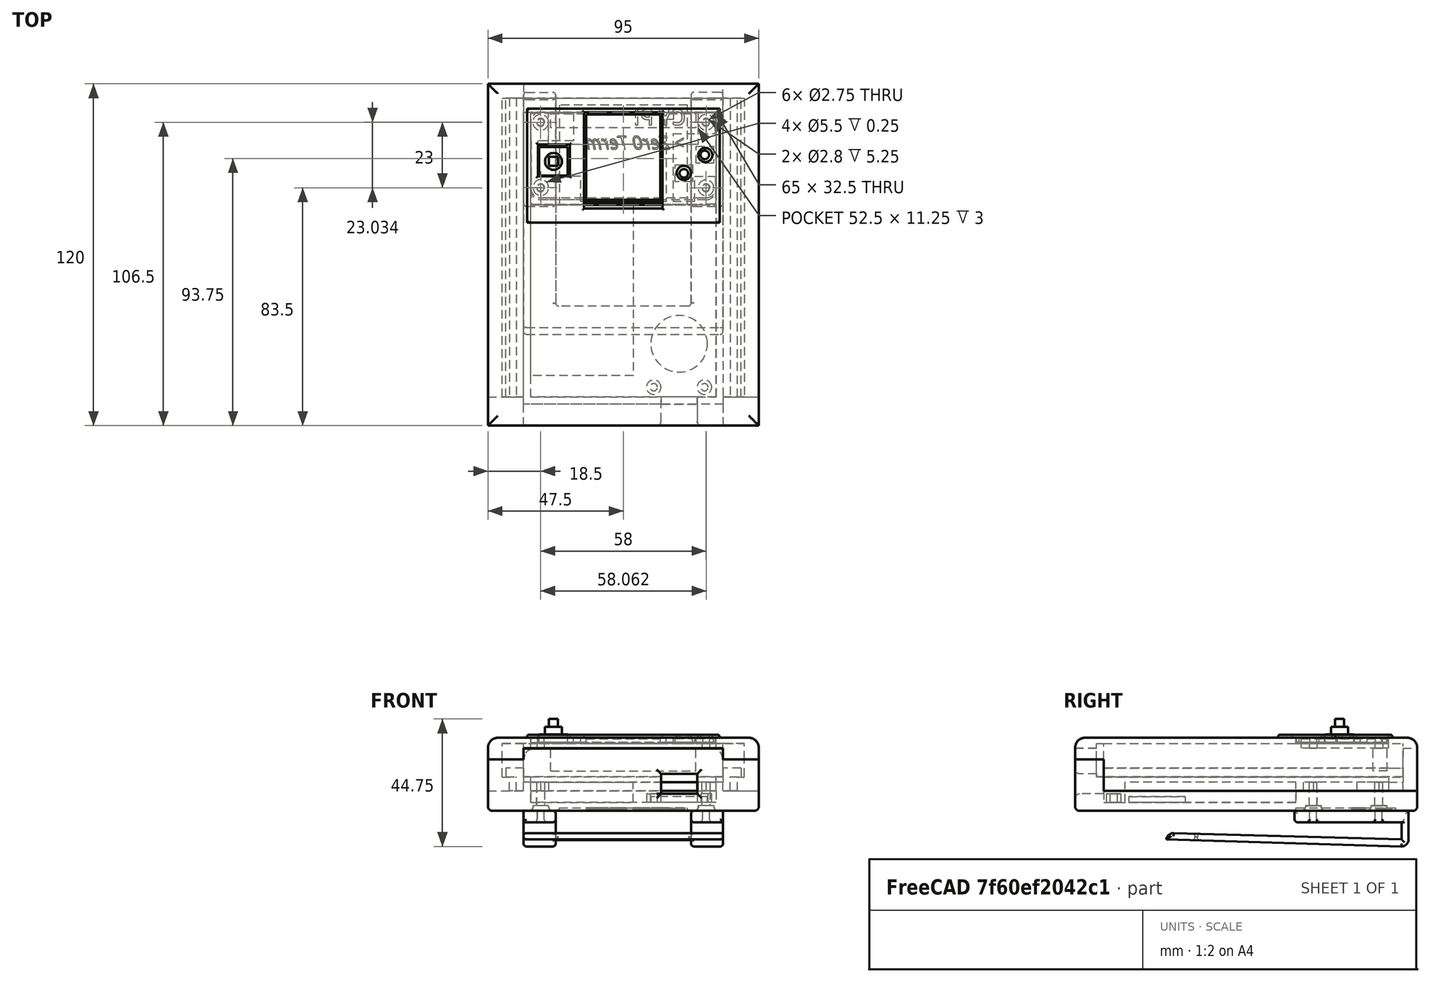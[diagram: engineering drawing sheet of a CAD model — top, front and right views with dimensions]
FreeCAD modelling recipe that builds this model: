
FCSTD DOCUMENT  (FreeCAD 0.18R4 (GitTag))
Label: ZeroDay-Dexk
License: All rights reserved
LicenseURL: http://en.wikipedia.org/wiki/All_rights_reserved
objects: Sketcher::SketchObject×37, PartDesign::Pad×28, PartDesign::Pocket×10, PartDesign::Fillet×9, PartDesign::Body×6, App::DocumentObjectGroup×3, Mesh::Feature×2, Part::Part2DObjectPython×2, Part::Extrusion×2, App::MeasureDistance×2
note: 132 computed .brp shape members not serialized (recipe doc carries the construction recipe); baked Part::Feature solids carry a one-line shape summary decoded from their .brp

FEATURE [Mesh::Feature] RaspberryPiZeroW
  Placement = pos=(0,0,0) rot=(1,0,0;1.5708rad)
FEATURE [Sketcher::SketchObject] Sketch
  MapMode = 5
  Placement = pos=(0,0,0) rot=(1,0,0;1.5708rad)
  Support = -> [XZ_Plane]
  sketch-geometry (18):
    g0: LineSegment [constr] StartX=0 StartY=0 StartZ=0 EndX=65 EndY=0 EndZ=0
    g1: LineSegment [constr] StartX=65 StartY=0 StartZ=0 EndX=65 EndY=30 EndZ=0
    g2: LineSegment [constr] StartX=65 StartY=30 StartZ=0 EndX=0 EndY=30 EndZ=0
    g3: LineSegment [constr] StartX=0 StartY=30 StartZ=0 EndX=0 EndY=0 EndZ=0
    g4: Circle CenterX=3.5 CenterY=26.5 CenterZ=0 NormalX=0 NormalY=0 NormalZ=1 AngleXU=0 Radius=1.375
    g5: Circle CenterX=61.5 CenterY=26.5 CenterZ=0 NormalX=0 NormalY=0 NormalZ=1 AngleXU=0 Radius=1.375
    g6: Circle CenterX=3.5 CenterY=3.5 CenterZ=0 NormalX=0 NormalY=0 NormalZ=1 AngleXU=0 Radius=1.375
    g7: Circle CenterX=61.5 CenterY=3.5 CenterZ=0 NormalX=0 NormalY=0 NormalZ=1 AngleXU=0 Radius=1.375
    g8: LineSegment StartX=6.25 StartY=0 StartZ=0 EndX=0 EndY=0 EndZ=0
    g9: LineSegment StartX=0 StartY=0 StartZ=0 EndX=0 EndY=30 EndZ=0
    g10: LineSegment StartX=0 StartY=30 StartZ=0 EndX=6.25 EndY=30 EndZ=0
    g11: LineSegment StartX=6.25 StartY=11.25 StartZ=0 EndX=6.25 EndY=0 EndZ=0
    g12: LineSegment StartX=6.25 StartY=30 StartZ=0 EndX=58.75 EndY=30 EndZ=0
    g13: LineSegment StartX=58.75 StartY=11.25 StartZ=0 EndX=6.25 EndY=11.25 EndZ=0
    g14: LineSegment StartX=65 StartY=0 StartZ=0 EndX=58.75 EndY=0 EndZ=0
    g15: LineSegment StartX=58.75 StartY=0 StartZ=0 EndX=58.75 EndY=11.25 EndZ=0
    g16: LineSegment StartX=58.75 StartY=30 StartZ=0 EndX=65 EndY=30 EndZ=0
    g17: LineSegment StartX=65 StartY=30 StartZ=0 EndX=65 EndY=0 EndZ=0
  constraints (38):
    c: Coincident(g0,g1)
    c: Coincident(g1,g2)
    c: Coincident(g2,g3)
    c: Coincident(g3,g0)
    c: Horizontal(g0)
    c: Horizontal(g2)
    c: Vertical(g1)
    c: Vertical(g3)
    c: DistanceY(g4,g2) = 3.5
    c: DistanceY(g0,g6) = 3.5
    c: DistanceY(g5,g1) = 3.5
    c: DistanceY(g0,g7) = 3.5
    c: DistanceX(g0,g6) = 3.5
    c: DistanceX(g2,g4) = 3.5
    c: DistanceX(g7,g0) = 3.5
    c: DistanceX(g5,g1) = 3.5
    c: Radius(g4) = 1.375
    c: Radius(g6) = 1.375
    c: Radius(g7) = 1.375
    c: Radius(g5) = 1.375
    c: Coincident(g8,g9)
    c: Coincident(g9,g10)
    c: Coincident(g11,g8)
    c: Horizontal(g8)
    c: Horizontal(g10)
    c: Vertical(g9)
    c: Vertical(g11)
    c: Horizontal(g12)
    c: Horizontal(g13)
    c: Coincident(g14,g15)
    c: Coincident(g16,g17)
    c: Coincident(g17,g14)
    c: Horizontal(g14)
    c: Horizontal(g16)
    c: Vertical(g15)
    c: Vertical(g17)
    c: PointOnObject(g15,g13)
    c: PointOnObject(g11,g13)
FEATURE [PartDesign::Pad] Pad
  Length = 3
  Length2 = 100
  Placement = pos=(0,0,0) rot=(1,0,0;1.5708rad)
  Profile = -> Sketch
  Type = 0
FEATURE [PartDesign::Fillet] Fillet
  Base = -> Pad [Edge5,Edge2,Edge14,Edge17]
  BaseFeature = -> Pad
  Placement = pos=(0,0,0) rot=(1,0,0;1.5708rad)
  Radius = 3.5
FEATURE [Sketcher::SketchObject] Sketch001
  ExternalGeometry = -> [Fillet]
  MapMode = 5
  Placement = pos=(0,-3,1.3e-15) rot=(1,0,0;1.5708rad)
  Support = -> [Fillet]
  sketch-geometry (8):
    g0: LineSegment StartX=-15 StartY=-10 StartZ=0 EndX=80 EndY=-10 EndZ=0
    g1: LineSegment StartX=80 StartY=-10 StartZ=0 EndX=80 EndY=110 EndZ=0
    g2: LineSegment StartX=80 StartY=110 StartZ=0 EndX=-15 EndY=110 EndZ=0
    g3: LineSegment StartX=-15 StartY=110 StartZ=0 EndX=-15 EndY=-10 EndZ=0
    g4: Circle CenterX=3.5 CenterY=26.5 CenterZ=0 NormalX=0 NormalY=0 NormalZ=1 AngleXU=0 Radius=1.375
    g5: Circle CenterX=3.5 CenterY=3.5 CenterZ=0 NormalX=0 NormalY=0 NormalZ=1 AngleXU=0 Radius=1.4
    g6: Circle CenterX=61.5 CenterY=3.5 CenterZ=0 NormalX=0 NormalY=0 NormalZ=1 AngleXU=0 Radius=1.4
    g7: Circle CenterX=61.5 CenterY=26.5 CenterZ=0 NormalX=0 NormalY=0 NormalZ=1 AngleXU=0 Radius=1.40357
  constraints (13):
    c: Coincident(g0,g1)
    c: Coincident(g1,g2)
    c: Coincident(g2,g3)
    c: Coincident(g3,g0)
    c: Horizontal(g0)
    c: Horizontal(g2)
    c: Vertical(g1)
    c: Vertical(g3)
    c: Radius(g-5) = 1.375
    c: Radius(g-5) = 1.375
    c: Radius(g4) = 1.375
    c: Distance(g0) = 95
    c: Distance(g1) = 120
FEATURE [PartDesign::Pad] Pad001
  BaseFeature = -> Fillet
  Length = 7
  Length2 = 100
  Placement = pos=(0,0,0) rot=(1,0,0;1.5708rad)
  Profile = -> Sketch001
  Type = 0
FEATURE [Sketcher::SketchObject] Sketch002
  ExternalGeometry = -> [Pad001]
  MapMode = 5
  Placement = pos=(0,-10,1e-14) rot=(1,0,0;1.5708rad)
  Support = -> [Pad001]
  sketch-geometry (4):
    g0: Circle CenterX=3.5 CenterY=3.5 CenterZ=0 NormalX=0 NormalY=0 NormalZ=1 AngleXU=0 Radius=2.75
    g1: Circle CenterX=3.55131 CenterY=26.4052 CenterZ=0 NormalX=0 NormalY=0 NormalZ=1 AngleXU=0 Radius=2.75
    g2: Circle CenterX=61.5 CenterY=26.5 CenterZ=0 NormalX=0 NormalY=0 NormalZ=1 AngleXU=0 Radius=2.75
    g3: Circle CenterX=61.5615 CenterY=3.46611 CenterZ=0 NormalX=0 NormalY=0 NormalZ=1 AngleXU=0 Radius=2.75
  constraints (4):
    c: Radius(g2) = 2.75
    c: Radius(g3) = 2.75
    c: Radius(g0) = 2.75
    c: Radius(g1) = 2.75
FEATURE [PartDesign::Pocket] Pocket
  BaseFeature = -> Pad001
  Length = 1.75
  Length2 = 100
  Placement = pos=(0,0,0) rot=(1,0,0;1.5708rad)
  Profile = -> Sketch002
  Type = 0
FEATURE [Sketcher::SketchObject] Sketch003
  MapMode = 5
  Placement = pos=(0,-3,3e-15) rot=(-1,0,0;1.5708rad)
  Support = -> [Pocket]
  sketch-geometry (4):
    g0: LineSegment StartX=0 StartY=-32.5 StartZ=0 EndX=65 EndY=-32.5 EndZ=0
    g1: LineSegment StartX=65 StartY=-32.5 StartZ=0 EndX=65 EndY=-100 EndZ=0
    g2: LineSegment StartX=65 StartY=-100 StartZ=0 EndX=0 EndY=-100 EndZ=0
    g3: LineSegment StartX=0 StartY=-100 StartZ=0 EndX=0 EndY=-32.5 EndZ=0
  constraints (8):
    c: Coincident(g0,g1)
    c: Coincident(g1,g2)
    c: Coincident(g2,g3)
    c: Coincident(g3,g0)
    c: Horizontal(g0)
    c: Horizontal(g2)
    c: Vertical(g1)
    c: Vertical(g3)
FEATURE [PartDesign::Pocket] Pocket001
  BaseFeature = -> Pocket
  Length = 4
  Length2 = 100
  Placement = pos=(0,0,0) rot=(1,0,0;1.5708rad)
  Profile = -> Sketch003
  Type = 0
FEATURE [Sketcher::SketchObject] Sketch004
  MapMode = 5
  Placement = pos=(0,-3,3e-15) rot=(-1,0,0;1.5708rad)
  Support = -> [Pocket001]
  sketch-geometry (14):
    g0: LineSegment StartX=0 StartY=5 StartZ=0 EndX=65 EndY=5 EndZ=0
    g1: LineSegment StartX=65 StartY=0 StartZ=0 EndX=0 EndY=0 EndZ=0
    g2: LineSegment StartX=80 StartY=-110 StartZ=0 EndX=-15 EndY=-110 EndZ=0
    g3: LineSegment StartX=-15 StartY=-110 StartZ=0 EndX=-15 EndY=-100 EndZ=0
    g4: LineSegment StartX=-15 StartY=-100 StartZ=0 EndX=-5 EndY=-100 EndZ=0
    g5: LineSegment StartX=80 StartY=-100 StartZ=0 EndX=80 EndY=-110 EndZ=0
    g6: LineSegment StartX=0 StartY=5 StartZ=0 EndX=-5 EndY=5 EndZ=0
    g7: LineSegment StartX=-5 StartY=5 StartZ=0 EndX=-5 EndY=-100 EndZ=0
    g8: LineSegment StartX=0 StartY=-100 StartZ=0 EndX=0 EndY=0 EndZ=0
    g9: LineSegment StartX=65 StartY=5 StartZ=0 EndX=70 EndY=5 EndZ=0
    g10: LineSegment StartX=70 StartY=5 StartZ=0 EndX=70 EndY=-100 EndZ=0
    g11: LineSegment StartX=65 StartY=-100 StartZ=0 EndX=65 EndY=0 EndZ=0
    g12: LineSegment StartX=70 StartY=-100 StartZ=0 EndX=80 EndY=-100 EndZ=0
    g13: LineSegment StartX=0 StartY=-100 StartZ=0 EndX=65 EndY=-100 EndZ=0
  constraints (24):
    c: Horizontal(g0)
    c: Horizontal(g1)
    c: Coincident(g2,g3)
    c: Coincident(g3,g4)
    c: Coincident(g12,g5)
    c: Coincident(g5,g2)
    c: Horizontal(g2)
    c: Horizontal(g4)
    c: Vertical(g3)
    c: Vertical(g5)
    c: Coincident(g6,g7)
    c: Horizontal(g6)
    c: Vertical(g7)
    c: Vertical(g8)
    c: Coincident(g9,g10)
    c: Horizontal(g9)
    c: Vertical(g10)
    c: Vertical(g11)
    c: PointOnObject(g12,g10)
    c: Tangent(g4,g12)
    c: PointOnObject(g4,g7)
    c: Tangent(g4,g13)
    c: PointOnObject(g8,g1)
    c: PointOnObject(g11,g1)
FEATURE [PartDesign::Pad] Pad002
  BaseFeature = -> Pocket001
  Length = 5
  Length2 = 100
  Placement = pos=(0,0,0) rot=(1,0,0;1.5708rad)
  Profile = -> Sketch004
  Type = 0
FEATURE [Sketcher::SketchObject] Sketch005
  MapMode = 5
  Placement = pos=(0,2,-4.4e-15) rot=(-1,0,0;1.5708rad)
  Support = -> [Pad002]
  sketch-geometry (12):
    g0: LineSegment StartX=75 StartY=5 StartZ=0 EndX=-10 EndY=5 EndZ=0
    g1: LineSegment StartX=-10 StartY=5 StartZ=0 EndX=-10 EndY=-100 EndZ=0
    g2: LineSegment StartX=-15 StartY=-100 StartZ=0 EndX=-10 EndY=-100 EndZ=0
    g3: LineSegment StartX=-15 StartY=-100 StartZ=0 EndX=-15 EndY=-110 EndZ=0
    g4: LineSegment StartX=-15 StartY=-110 StartZ=0 EndX=80 EndY=-110 EndZ=0
    g5: LineSegment StartX=80 StartY=-100 StartZ=0 EndX=80 EndY=-110 EndZ=0
    g6: LineSegment StartX=80 StartY=-100 StartZ=0 EndX=75 EndY=-100 EndZ=0
    g7: LineSegment StartX=75 StartY=-100 StartZ=0 EndX=75 EndY=5 EndZ=0
    g8: LineSegment StartX=-2.5 StartY=0 StartZ=0 EndX=67.5 EndY=0 EndZ=0
    g9: LineSegment StartX=67.5 StartY=0 StartZ=0 EndX=67.5 EndY=-102.5 EndZ=0
    g10: LineSegment StartX=67.5 StartY=-102.5 StartZ=0 EndX=-2.5 EndY=-102.5 EndZ=0
    g11: LineSegment StartX=-2.5 StartY=-102.5 StartZ=0 EndX=-2.5 EndY=0 EndZ=0
  constraints (8):
    c: Coincident(g8,g9)
    c: Coincident(g9,g10)
    c: Coincident(g10,g11)
    c: Coincident(g11,g8)
    c: Horizontal(g8)
    c: Horizontal(g10)
    c: Vertical(g9)
    c: Vertical(g11)
FEATURE [PartDesign::Pad] Pad003
  BaseFeature = -> Pad002
  Length = 3
  Length2 = 100
  Placement = pos=(0,0,0) rot=(1,0,0;1.5708rad)
  Profile = -> Sketch005
  Type = 0
FEATURE [Sketcher::SketchObject] Sketch006
  MapMode = 5
  Placement = pos=(0,5,-1.33e-14) rot=(-1,0,0;1.5708rad)
  Support = -> [Pad003]
  sketch-geometry (4):
    g0: LineSegment StartX=-2.5 StartY=0 StartZ=0 EndX=67.5 EndY=0 EndZ=0
    g1: LineSegment StartX=67.5 StartY=0 StartZ=0 EndX=67.5 EndY=5 EndZ=0
    g2: LineSegment StartX=67.5 StartY=5 StartZ=0 EndX=-2.5 EndY=5 EndZ=0
    g3: LineSegment StartX=-2.5 StartY=5 StartZ=0 EndX=-2.5 EndY=0 EndZ=0
  constraints (8):
    c: Coincident(g0,g1)
    c: Coincident(g1,g2)
    c: Coincident(g2,g3)
    c: Coincident(g3,g0)
    c: Horizontal(g0)
    c: Horizontal(g2)
    c: Vertical(g1)
    c: Vertical(g3)
FEATURE [PartDesign::Pocket] Pocket002
  BaseFeature = -> Pad003
  Length = 5
  Length2 = 100
  Placement = pos=(0,0,0) rot=(1,0,0;1.5708rad)
  Profile = -> Sketch006
  Type = 0
FEATURE [PartDesign::Fillet] Fillet001
  Base = -> Pocket002 [Face79]
  BaseFeature = -> Pocket002
  Placement = pos=(0,0,0) rot=(1,0,0;1.5708rad)
  Radius = 1.5
FEATURE [Sketcher::SketchObject] Sketch007
  MapMode = 5
  Placement = pos=(0,2.752e-13,110) rot=(0,0,1;3.14159rad)
  Support = -> [Fillet001]
FEATURE [Sketcher::SketchObject] Sketch008
  MapMode = 5
  Placement = pos=(0,-7,1.4e-14) rot=(-1,0,0;1.5708rad)
  Support = -> [Fillet001]
  sketch-geometry (9):
    g0: LineSegment [constr] StartX=63.5 StartY=-99.06 StartZ=0 EndX=40.64 EndY=-99.06 EndZ=0
    g1: LineSegment [constr] StartX=40.64 StartY=-99.06 StartZ=0 EndX=40.64 EndY=-63.5 EndZ=0
    g2: LineSegment [constr] StartX=40.64 StartY=-63.5 StartZ=0 EndX=63.5 EndY=-63.5 EndZ=0
    g3: LineSegment [constr] StartX=63.5 StartY=-63.5 StartZ=0 EndX=63.5 EndY=-99.06 EndZ=0
    g4: Circle CenterX=43.18 CenterY=-96.52 CenterZ=0 NormalX=0 NormalY=0 NormalZ=1 AngleXU=0 Radius=1.27
    g5: Circle CenterX=60.96 CenterY=-96.52 CenterZ=0 NormalX=0 NormalY=0 NormalZ=1 AngleXU=0 Radius=1.27
    g6: Circle CenterX=43.18 CenterY=-96.52 CenterZ=0 NormalX=0 NormalY=0 NormalZ=1 AngleXU=0 Radius=2.54
    g7: Circle CenterX=60.96 CenterY=-96.52 CenterZ=0 NormalX=0 NormalY=0 NormalZ=1 AngleXU=0 Radius=2.54
    g8: Circle CenterX=52.07 CenterY=-81.28 CenterZ=0 NormalX=0 NormalY=0 NormalZ=1 AngleXU=0 Radius=9.91902
  constraints (10):
    c: Coincident(g0,g1)
    c: Coincident(g1,g2)
    c: Coincident(g2,g3)
    c: Coincident(g3,g0)
    c: Horizontal(g0)
    c: Horizontal(g2)
    c: Vertical(g1)
    c: Vertical(g3)
    c: Radius(g5) = 1.27
    c: Radius(g4) = 1.27
FEATURE [PartDesign::Pad] Pad004
  BaseFeature = -> Fillet001
  Length = 2
  Length2 = 100
  Placement = pos=(0,0,0) rot=(1,0,0;1.5708rad)
  Profile = -> Sketch008
  Type = 0
FEATURE [PartDesign::Pad] Pad005
  BaseFeature = -> Pad004
  Length = 1
  Length2 = 100
  Placement = pos=(0,0,0) rot=(1,0,0;1.5708rad)
  Profile = -> Pad004 [Face95]
  Type = 0
FEATURE [PartDesign::Pad] Pad006
  BaseFeature = -> Pad005
  Length = 1
  Length2 = 100
  Placement = pos=(0,0,0) rot=(1,0,0;1.5708rad)
  Profile = -> Pad005 [Face94]
  Type = 0
FEATURE [Sketcher::SketchObject] Sketch009
  MapMode = 5
  Placement = pos=(0,2,-4.4e-15) rot=(-1,0,0;1.5708rad)
  Support = -> [Pad006]
  sketch-geometry (8):
    g0: LineSegment [constr] StartX=40.64 StartY=-99.06 StartZ=0 EndX=63.5 EndY=-99.06 EndZ=0
    g1: LineSegment [constr] StartX=63.5 StartY=-99.06 StartZ=0 EndX=63.5 EndY=-58.42 EndZ=0
    g2: LineSegment [constr] StartX=63.5 StartY=-58.42 StartZ=0 EndX=40.64 EndY=-58.42 EndZ=0
    g3: LineSegment [constr] StartX=40.64 StartY=-58.42 StartZ=0 EndX=40.64 EndY=-99.06 EndZ=0
    g4: LineSegment StartX=45.72 StartY=-99.06 StartZ=0 EndX=58.42 EndY=-99.06 EndZ=0
    g5: LineSegment StartX=58.42 StartY=-99.06 StartZ=0 EndX=58.42 EndY=-111.76 EndZ=0
    g6: LineSegment StartX=58.42 StartY=-111.76 StartZ=0 EndX=45.72 EndY=-111.76 EndZ=0
    g7: LineSegment StartX=45.72 StartY=-111.76 StartZ=0 EndX=45.72 EndY=-99.06 EndZ=0
  constraints (16):
    c: Coincident(g0,g1)
    c: Coincident(g1,g2)
    c: Coincident(g2,g3)
    c: Coincident(g3,g0)
    c: Horizontal(g0)
    c: Horizontal(g2)
    c: Vertical(g1)
    c: Vertical(g3)
    c: Coincident(g4,g5)
    c: Coincident(g5,g6)
    c: Coincident(g6,g7)
    c: Coincident(g7,g4)
    c: Horizontal(g4)
    c: Horizontal(g6)
    c: Vertical(g5)
    c: Vertical(g7)
FEATURE [PartDesign::Pocket] Pocket003
  BaseFeature = -> Pad006
  Length = 6
  Length2 = 1
  Placement = pos=(0,0,0) rot=(1,0,0;1.5708rad)
  Profile = -> Sketch009
  Type = 4
FEATURE [PartDesign::Fillet] Fillet002
  Base = -> Pocket003 [Edge49,Edge9,Edge32,Edge85]
  BaseFeature = -> Pocket003
  Placement = pos=(0,0,0) rot=(1,0,0;1.5708rad)
  Radius = 1.5
FEATURE [Sketcher::SketchObject] Sketch010
  MapMode = 5
  Placement = pos=(0,5,-1.33e-14) rot=(-1,0,0;1.5708rad)
  Support = -> [Fillet002]
  sketch-geometry (12):
    g0: LineSegment StartX=-15 StartY=-100 StartZ=0 EndX=-2.5 EndY=-100 EndZ=0
    g1: LineSegment StartX=-2.5 StartY=-100 StartZ=0 EndX=-2.5 EndY=-110 EndZ=0
    g2: LineSegment StartX=-2.5 StartY=-110 StartZ=0 EndX=-15 EndY=-110 EndZ=0
    g3: LineSegment StartX=-15 StartY=-110 StartZ=0 EndX=-15 EndY=-100 EndZ=0
    g4: LineSegment StartX=-2.5 StartY=-102.5 StartZ=0 EndX=67.5 EndY=-102.5 EndZ=0
    g5: LineSegment StartX=67.5 StartY=-102.5 StartZ=0 EndX=67.5 EndY=-110 EndZ=0
    g6: LineSegment StartX=67.5 StartY=-110 StartZ=0 EndX=-2.5 EndY=-110 EndZ=0
    g7: LineSegment StartX=-2.5 StartY=-110 StartZ=0 EndX=-2.5 EndY=-102.5 EndZ=0
    g8: LineSegment StartX=67.5 StartY=-100 StartZ=0 EndX=80 EndY=-100 EndZ=0
    g9: LineSegment StartX=80 StartY=-100 StartZ=0 EndX=80 EndY=-110 EndZ=0
    g10: LineSegment StartX=80 StartY=-110 StartZ=0 EndX=67.5 EndY=-110 EndZ=0
    g11: LineSegment StartX=67.5 StartY=-110 StartZ=0 EndX=67.5 EndY=-100 EndZ=0
  constraints (24):
    c: Coincident(g0,g1)
    c: Coincident(g1,g2)
    c: Coincident(g2,g3)
    c: Coincident(g3,g0)
    c: Horizontal(g0)
    c: Horizontal(g2)
    c: Vertical(g1)
    c: Vertical(g3)
    c: Coincident(g4,g5)
    c: Coincident(g5,g6)
    c: Coincident(g6,g7)
    c: Coincident(g7,g4)
    c: Horizontal(g4)
    c: Horizontal(g6)
    c: Vertical(g5)
    c: Vertical(g7)
    c: Coincident(g8,g9)
    c: Coincident(g9,g10)
    c: Coincident(g10,g11)
    c: Coincident(g11,g8)
    c: Horizontal(g8)
    c: Horizontal(g10)
    c: Vertical(g9)
    c: Vertical(g11)
FEATURE [PartDesign::Pad] Pad007
  BaseFeature = -> Fillet002
  Length = 3
  Length2 = 100
  Placement = pos=(0,0,0) rot=(1,0,0;1.5708rad)
  Profile = -> Sketch010
  Type = 0
FEATURE [Sketcher::SketchObject] Sketch011
  MapMode = 5
  Support = -> [XY_Plane001]
  sketch-geometry (10):
    g0: LineSegment StartX=0 StartY=0 StartZ=0 EndX=95 EndY=0 EndZ=0
    g1: LineSegment StartX=95 StartY=0 StartZ=0 EndX=95 EndY=-5 EndZ=0
    g2: LineSegment StartX=86.25 StartY=-5 StartZ=0 EndX=8.75 EndY=-5 EndZ=0
    g3: LineSegment StartX=0 StartY=-5 StartZ=0 EndX=0 EndY=0 EndZ=0
    g4: LineSegment StartX=86.25 StartY=-5 StartZ=0 EndX=86.25 EndY=-110 EndZ=0
    g5: LineSegment StartX=86.25 StartY=-110 StartZ=0 EndX=95 EndY=-110 EndZ=0
    g6: LineSegment StartX=95 StartY=-110 StartZ=0 EndX=95 EndY=-5 EndZ=0
    g7: LineSegment StartX=0 StartY=-5 StartZ=0 EndX=0 EndY=-110 EndZ=0
    g8: LineSegment StartX=0 StartY=-110 StartZ=0 EndX=8.75 EndY=-110 EndZ=0
    g9: LineSegment StartX=8.75 StartY=-110 StartZ=0 EndX=8.75 EndY=-5 EndZ=0
  constraints (18):
    c: Coincident(g0,g1)
    c: Coincident(g3,g0)
    c: Horizontal(g0)
    c: Horizontal(g2)
    c: Vertical(g1)
    c: Vertical(g3)
    c: Coincident(g0,g-1)
    c: Coincident(g4,g5)
    c: Coincident(g5,g6)
    c: Horizontal(g5)
    c: Vertical(g4)
    c: Vertical(g6)
    c: Coincident(g7,g8)
    c: Coincident(g8,g9)
    c: Horizontal(g8)
    c: Vertical(g7)
    c: Vertical(g9)
    c: PointOnObject(g9,g2)
FEATURE [PartDesign::Pad] Pad008
  Length = 4.8
  Length2 = 100
  Profile = -> Sketch011
  Type = 0
FEATURE [Sketcher::SketchObject] Sketch012
  MapMode = 5
  Placement = pos=(0,0,4.8) rot=(0,0,1;0rad)
  Support = -> [Pad008]
  sketch-geometry (12):
    g0: LineSegment StartX=0 StartY=0 StartZ=0 EndX=5 EndY=0 EndZ=0
    g1: LineSegment StartX=5 StartY=0 StartZ=0 EndX=5 EndY=-110 EndZ=0
    g2: LineSegment StartX=5 StartY=-110 StartZ=0 EndX=0 EndY=-110 EndZ=0
    g3: LineSegment StartX=0 StartY=-110 StartZ=0 EndX=0 EndY=0 EndZ=0
    g4: LineSegment StartX=90 StartY=-110 StartZ=0 EndX=95 EndY=-110 EndZ=0
    g5: LineSegment StartX=95 StartY=-110 StartZ=0 EndX=95 EndY=-5 EndZ=0
    g6: LineSegment StartX=95 StartY=-5 StartZ=0 EndX=90 EndY=-5 EndZ=0
    g7: LineSegment StartX=90 StartY=-5 StartZ=0 EndX=90 EndY=-110 EndZ=0
    g8: LineSegment StartX=95 StartY=0 StartZ=0 EndX=5 EndY=0 EndZ=0
    g9: LineSegment StartX=5 StartY=0 StartZ=0 EndX=5 EndY=-5 EndZ=0
    g10: LineSegment StartX=5 StartY=-5 StartZ=0 EndX=95 EndY=-5 EndZ=0
    g11: LineSegment StartX=95 StartY=-5 StartZ=0 EndX=95 EndY=0 EndZ=0
  constraints (26):
    c: Coincident(g0,g1)
    c: Coincident(g1,g2)
    c: Coincident(g2,g3)
    c: Coincident(g3,g0)
    c: Horizontal(g0)
    c: Horizontal(g2)
    c: Vertical(g1)
    c: Vertical(g3)
    c: Coincident(g0,g-1)
    c: Coincident(g4,g5)
    c: Coincident(g5,g6)
    c: Coincident(g6,g7)
    c: Coincident(g7,g4)
    c: Horizontal(g4)
    c: Horizontal(g6)
    c: Vertical(g5)
    c: Vertical(g7)
    c: Coincident(g8,g9)
    c: Coincident(g9,g10)
    c: Coincident(g10,g11)
    c: Coincident(g11,g8)
    c: Horizontal(g8)
    c: Horizontal(g10)
    c: Vertical(g9)
    c: Vertical(g11)
    c: PointOnObject(g9,g1)
FEATURE [PartDesign::Pad] Pad009
  BaseFeature = -> Pad008
  Length = 0.2
  Length2 = 100
  Profile = -> Sketch012
  Type = 0
FEATURE [PartDesign::Pad] Pad010
  BaseFeature = -> Pad009
  Length = 6
  Length2 = 100
  Profile = -> Pad009 [Face16]
  Type = 0
FEATURE [Mesh::Feature] _0x2_pin_header  label="20x2 pin header"
  Placement = pos=(32.5,-3,1.5) rot=(0,0,1;4.71239rad)
FEATURE [Sketcher::SketchObject] Sketch013
  MapMode = 5
  Support = -> [XY_Plane002]
  sketch-geometry (4):
    g0: LineSegment StartX=7 StartY=-0.5 StartZ=0 EndX=58 EndY=-0.5 EndZ=0
    g1: LineSegment StartX=58 StartY=-0.5 StartZ=0 EndX=58 EndY=-5.5 EndZ=0
    g2: LineSegment StartX=58 StartY=-5.5 StartZ=0 EndX=7 EndY=-5.5 EndZ=0
    g3: LineSegment StartX=7 StartY=-5.5 StartZ=0 EndX=7 EndY=-0.5 EndZ=0
  constraints (8):
    c: Coincident(g0,g1)
    c: Coincident(g1,g2)
    c: Coincident(g2,g3)
    c: Coincident(g3,g0)
    c: Horizontal(g0)
    c: Horizontal(g2)
    c: Vertical(g1)
    c: Vertical(g3)
FEATURE [PartDesign::Pad] Pad011
  Length = 8
  Length2 = 100
  Profile = -> Sketch013
  Type = 0
FEATURE [Sketcher::SketchObject] Sketch014
  MapMode = 5
  Placement = pos=(0,0,8) rot=(0,0,1;0rad)
  Support = -> [Pad011]
  sketch-geometry (8):
    g0: LineSegment StartX=0 StartY=0 StartZ=0 EndX=65 EndY=0 EndZ=0
    g1: LineSegment StartX=65 StartY=0 StartZ=0 EndX=65 EndY=-30.7 EndZ=0
    g2: LineSegment StartX=65 StartY=-30.7 StartZ=0 EndX=0 EndY=-30.7 EndZ=0
    g3: LineSegment StartX=0 StartY=-30.7 StartZ=0 EndX=0 EndY=0 EndZ=0
    g4: Circle CenterX=3.5 CenterY=-3.5 CenterZ=0 NormalX=0 NormalY=0 NormalZ=1 AngleXU=0 Radius=1.375
    g5: Circle CenterX=61.5 CenterY=-3.5 CenterZ=0 NormalX=0 NormalY=0 NormalZ=1 AngleXU=0 Radius=1.375
    g6: Circle CenterX=61.5 CenterY=-26.5 CenterZ=0 NormalX=0 NormalY=0 NormalZ=1 AngleXU=0 Radius=1.375
    g7: Circle CenterX=3.5 CenterY=-26.5 CenterZ=0 NormalX=0 NormalY=0 NormalZ=1 AngleXU=0 Radius=1.375
  constraints (23):
    c: Coincident(g0,g1)
    c: Coincident(g1,g2)
    c: Coincident(g2,g3)
    c: Coincident(g3,g0)
    c: Horizontal(g0)
    c: Horizontal(g2)
    c: Vertical(g1)
    c: Vertical(g3)
    c: Coincident(g0,g-1)
    c: Distance(g1) = 30.7
    c: Radius(g7) = 1.375
    c: Radius(g4) = 1.375
    c: Radius(g5) = 1.375
    c: Radius(g6) = 1.375
    c: DistanceX(g0,g4) = 3.5
    c: DistanceX(g5,g0) = 3.5
    c: DistanceX(g6,g1) = 3.5
    c: DistanceX(g2,g7) = 3.5
    c: Distance(g0) = 65
    c: DistanceY(g5,g0) = 3.5
    c: DistanceY(g4,g0) = 3.5
    c: DistanceY(g1,g6) = 4.2
    c: DistanceY(g2,g7) = 4.2
FEATURE [PartDesign::Pad] Pad012
  BaseFeature = -> Pad011
  Length = 1.651
  Length2 = 100
  Profile = -> Sketch014
  Type = 0
FEATURE [PartDesign::Fillet] Fillet003
  Base = -> Pad012 [Edge1,Edge5,Edge8,Edge2]
  BaseFeature = -> Pad012
  Radius = 3.5
FEATURE [Sketcher::SketchObject] Sketch015
  MapMode = 5
  Placement = pos=(0,-10,1e-14) rot=(1,0,0;1.5708rad)
  Support = -> [Pad007]
  sketch-geometry (4):
    g0: LineSegment StartX=55 StartY=-2.5 StartZ=0 EndX=10 EndY=-2.5 EndZ=0
    g1: LineSegment StartX=10 StartY=-2.5 StartZ=0 EndX=10 EndY=32.5 EndZ=0
    g2: LineSegment StartX=10 StartY=32.5 StartZ=0 EndX=55 EndY=32.5 EndZ=0
    g3: LineSegment StartX=55 StartY=32.5 StartZ=0 EndX=55 EndY=-2.5 EndZ=0
  constraints (8):
    c: Coincident(g0,g1)
    c: Coincident(g1,g2)
    c: Coincident(g2,g3)
    c: Coincident(g3,g0)
    c: Horizontal(g0)
    c: Horizontal(g2)
    c: Vertical(g1)
    c: Vertical(g3)
FEATURE [PartDesign::Pocket] Pocket004
  BaseFeature = -> Pad007
  Length = 1
  Length2 = 100
  Placement = pos=(0,0,0) rot=(1,0,0;1.5708rad)
  Profile = -> Sketch015
  Type = 0
FEATURE [Sketcher::SketchObject] Sketch017
  ExternalGeometry = -> [Fillet003]
  MapMode = 5
  Placement = pos=(0,0,9.651) rot=(0,0,1;0rad)
  Support = -> [Fillet003]
  sketch-geometry (5):
    g0: LineSegment StartX=3 StartY=-22.24 StartZ=0 EndX=13 EndY=-22.24 EndZ=0
    g1: LineSegment StartX=13 StartY=-22.24 StartZ=0 EndX=13 EndY=-12.24 EndZ=0
    g2: LineSegment StartX=13 StartY=-12.24 StartZ=0 EndX=3 EndY=-12.24 EndZ=0
    g3: LineSegment StartX=3 StartY=-12.24 StartZ=0 EndX=3 EndY=-22.24 EndZ=0
    g4: GeomPoint X=8 Y=-17.24 Z=0
  constraints (14):
    c: Coincident(g0,g1)
    c: Coincident(g1,g2)
    c: Coincident(g2,g3)
    c: Coincident(g3,g0)
    c: Horizontal(g0)
    c: Horizontal(g2)
    c: Vertical(g1)
    c: Vertical(g3)
    c: Distance(g1) = 10
    c: Distance(g0) = 10
    c: DistanceX(g4,g1) = 5
    c: DistanceX(g-4,g4) = 8
    c: DistanceY(g0,g4) = 5
    c: DistanceY(g-3,g4) = 13.46
FEATURE [PartDesign::Pad] Pad014
  BaseFeature = -> Fillet003
  Length = 3.15
  Length2 = 100
  Profile = -> Sketch017
  Type = 0
FEATURE [Sketcher::SketchObject] Sketch018
  ExternalGeometry = -> [Pad014]
  MapMode = 5
  Placement = pos=(0,0,12.801) rot=(0,0,1;0rad)
  Support = -> [Pad014]
  sketch-geometry (1):
    g0: Circle CenterX=8 CenterY=-17.24 CenterZ=0 NormalX=0 NormalY=0 NormalZ=1 AngleXU=0 Radius=2.975
  constraints (3):
    c: Radius(g0) = 2.975
    c: DistanceY(g0,g-4) = 5
    c: DistanceX(g0,g-4) = 5
FEATURE [PartDesign::Pad] Pad015
  BaseFeature = -> Pad014
  Length = 2.65
  Length2 = 100
  Profile = -> Sketch018
  Type = 0
FEATURE [Sketcher::SketchObject] Sketch019
  ExternalGeometry = -> [Pad015]
  MapMode = 5
  Placement = pos=(0,0,15.451) rot=(0,0,1;0rad)
  Support = -> [Pad015]
  sketch-geometry (4):
    g0: LineSegment StartX=6.4 StartY=-15.64 StartZ=0 EndX=9.6 EndY=-15.64 EndZ=0
    g1: LineSegment StartX=9.6 StartY=-15.64 StartZ=0 EndX=9.6 EndY=-18.84 EndZ=0
    g2: LineSegment StartX=9.6 StartY=-18.84 StartZ=0 EndX=6.4 EndY=-18.84 EndZ=0
    g3: LineSegment StartX=6.4 StartY=-18.84 StartZ=0 EndX=6.4 EndY=-15.64 EndZ=0
  constraints (12):
    c: Coincident(g0,g1)
    c: Coincident(g1,g2)
    c: Coincident(g2,g3)
    c: Coincident(g3,g0)
    c: Horizontal(g0)
    c: Horizontal(g2)
    c: Vertical(g1)
    c: Vertical(g3)
    c: Distance(g1) = 3.2
    c: Distance(g0) = 3.2
    c: DistanceY(g-3,g0) = 1.6
    c: DistanceX(g0,g-3) = 1.6
FEATURE [PartDesign::Pad] Pad016
  BaseFeature = -> Pad015
  Length = 2.8
  Length2 = 100
  Profile = -> Sketch019
  Type = 0
FEATURE [Sketcher::SketchObject] Sketch020
  ExternalGeometry = -> [Pad016]
  MapMode = 5
  Placement = pos=(0,0,9.651) rot=(0,0,1;0rad)
  Support = -> [Pad016]
  sketch-geometry (8):
    g0: LineSegment StartX=58.09 StartY=-11.95 StartZ=0 EndX=64.09 EndY=-11.95 EndZ=0
    g1: LineSegment StartX=64.09 StartY=-11.95 StartZ=0 EndX=64.09 EndY=-17.95 EndZ=0
    g2: LineSegment StartX=64.09 StartY=-17.95 StartZ=0 EndX=58.09 EndY=-17.95 EndZ=0
    g3: LineSegment StartX=58.09 StartY=-17.95 StartZ=0 EndX=58.09 EndY=-11.95 EndZ=0
    g4: LineSegment StartX=50.75 StartY=-18.43 StartZ=0 EndX=56.75 EndY=-18.43 EndZ=0
    g5: LineSegment StartX=56.75 StartY=-18.43 StartZ=0 EndX=56.75 EndY=-24.43 EndZ=0
    g6: LineSegment StartX=56.75 StartY=-24.43 StartZ=0 EndX=50.75 EndY=-24.43 EndZ=0
    g7: LineSegment StartX=50.75 StartY=-24.43 StartZ=0 EndX=50.75 EndY=-18.43 EndZ=0
  constraints (24):
    c: Coincident(g0,g1)
    c: Coincident(g1,g2)
    c: Coincident(g2,g3)
    c: Coincident(g3,g0)
    c: Horizontal(g0)
    c: Horizontal(g2)
    c: Vertical(g1)
    c: Vertical(g3)
    c: Coincident(g4,g5)
    c: Coincident(g5,g6)
    c: Coincident(g6,g7)
    c: Coincident(g7,g4)
    c: Horizontal(g4)
    c: Horizontal(g6)
    c: Vertical(g5)
    c: Vertical(g7)
    c: Distance(g5) = 6
    c: Distance(g6) = 6
    c: Distance(g3) = 6
    c: Distance(g0) = 6
    c: DistanceX(g0,g-3) = 0.91
    c: DistanceY(g-4,g1) = 12.75
    c: DistanceY(g-4,g5) = 6.27
    c: DistanceX(g4,g-3) = 8.25
FEATURE [PartDesign::Pad] Pad017
  BaseFeature = -> Pad016
  Length = 1.8
  Length2 = 100
  Profile = -> Sketch020
  Type = 0
FEATURE [Sketcher::SketchObject] Sketch021
  ExternalGeometry = -> [Pad017]
  MapMode = 5
  Placement = pos=(0,0,11.451) rot=(0,0,1;0rad)
  Support = -> [Pad017]
  sketch-geometry (2):
    g0: Circle CenterX=53.75 CenterY=-21.43 CenterZ=0 NormalX=0 NormalY=0 NormalZ=1 AngleXU=0 Radius=1.5
    g1: Circle CenterX=61.09 CenterY=-14.95 CenterZ=0 NormalX=0 NormalY=0 NormalZ=1 AngleXU=0 Radius=1.5
  constraints (6):
    c: Radius(g0) = 1.5
    c: Radius(g1) = 1.5
    c: DistanceX(g-6,g0) = 3
    c: DistanceX(g-4,g1) = 3
    c: DistanceY(g-6,g0) = 3
    c: DistanceY(g-4,g1) = 3
FEATURE [PartDesign::Pad] Pad018
  BaseFeature = -> Pad017
  Length = 1.3
  Length2 = 100
  Profile = -> Sketch021
  Type = 0
FEATURE [Sketcher::SketchObject] Sketch022
  ExternalGeometry = -> [Pad018]
  MapMode = 5
  Placement = pos=(0,0,9.651) rot=(0,0,1;0rad)
  Support = -> [Pad018]
  sketch-geometry (4):
    g0: LineSegment StartX=19.51 StartY=-0.7 StartZ=0 EndX=45.51 EndY=-0.7 EndZ=0
    g1: LineSegment StartX=45.51 StartY=-0.7 StartZ=0 EndX=45.51 EndY=-30.7 EndZ=0
    g2: LineSegment StartX=45.51 StartY=-30.7 StartZ=0 EndX=19.51 EndY=-30.7 EndZ=0
    g3: LineSegment StartX=19.51 StartY=-30.7 StartZ=0 EndX=19.51 EndY=-0.7 EndZ=0
  constraints (12):
    c: Coincident(g0,g1)
    c: Coincident(g1,g2)
    c: Coincident(g2,g3)
    c: Coincident(g3,g0)
    c: Horizontal(g0)
    c: Horizontal(g2)
    c: Vertical(g1)
    c: Vertical(g3)
    c: DistanceX(g-3,g2) = 19.51
    c: DistanceY(g-4,g2) = 0
    c: Distance(g1) = 30
    c: Distance(g0) = 26
FEATURE [PartDesign::Pad] Pad019
  BaseFeature = -> Pad018
  Length = 1.65
  Length2 = 100
  Profile = -> Sketch022
  Type = 0
FEATURE [PartDesign::Body] Body002  label="1.3 Color TFT Bonnet"
  Group = -> [Sketch013,Pad011,Sketch014,Pad012,Fillet003,Sketch017,Pad014,Sketch018,Pad015,Sketch019,Pad016,Sketch020,Pad017,Sketch021,Pad018,Sketch022,Pad019]
  Origin = -> Origin002
  Placement = pos=(0,0,4) rot=(0,0,1;0rad)
  Tip = -> Pad019
FEATURE [Sketcher::SketchObject] Sketch023
  MapMode = 5
  Support = -> [XY_Plane003]
  sketch-geometry (4):
    g0: LineSegment StartX=0 StartY=0 StartZ=0 EndX=36 EndY=0 EndZ=0
    g1: LineSegment StartX=36 StartY=0 StartZ=0 EndX=36 EndY=-60 EndZ=0
    g2: LineSegment StartX=36 StartY=-60 StartZ=0 EndX=0 EndY=-60 EndZ=0
    g3: LineSegment StartX=0 StartY=-60 StartZ=0 EndX=0 EndY=0 EndZ=0
  constraints (11):
    c: Coincident(g0,g1)
    c: Coincident(g1,g2)
    c: Coincident(g2,g3)
    c: Coincident(g3,g0)
    c: Horizontal(g0)
    c: Horizontal(g2)
    c: Vertical(g1)
    c: Vertical(g3)
    c: Coincident(g0,g-1)
    c: Distance(g2) = 36
    c: Distance(g1) = 60
FEATURE [PartDesign::Pad] Pad020
  Length = 7
  Length2 = 100
  Profile = -> Sketch023
  Type = 0
FEATURE [PartDesign::Body] Body003  label="Lipo 2000mAh"
  Group = -> [Sketch023,Pad020]
  Origin = -> Origin003
  Placement = pos=(0,-32.5,-7) rot=(0,0,1;0rad)
  Tip = -> Pad020
FEATURE [Sketcher::SketchObject] Sketch024
  MapMode = 5
  Placement = pos=(0,0,11) rot=(0,0,1;0rad)
  Support = -> [Pad010]
  sketch-geometry (12):
    g0: LineSegment StartX=0 StartY=0 StartZ=0 EndX=95 EndY=0 EndZ=0
    g1: LineSegment StartX=95 StartY=0 StartZ=0 EndX=95 EndY=-120 EndZ=0
    g2: LineSegment StartX=95 StartY=-120 StartZ=0 EndX=0 EndY=-120 EndZ=0
    g3: LineSegment StartX=0 StartY=-120 StartZ=0 EndX=0 EndY=0 EndZ=0
    g4: LineSegment StartX=5 StartY=-5 StartZ=0 EndX=90 EndY=-5 EndZ=0
    g5: LineSegment StartX=90 StartY=-5 StartZ=0 EndX=90 EndY=-110 EndZ=0
    g6: LineSegment StartX=90 StartY=-110 StartZ=0 EndX=82.5 EndY=-110 EndZ=0
    g7: LineSegment StartX=82.5 StartY=-110 StartZ=0 EndX=82.5 EndY=-112.5 EndZ=0
    g8: LineSegment StartX=82.5 StartY=-112.5 StartZ=0 EndX=12.5 EndY=-112.5 EndZ=0
    g9: LineSegment StartX=12.5 StartY=-112.5 StartZ=0 EndX=12.5 EndY=-110 EndZ=0
    g10: LineSegment StartX=12.5 StartY=-110 StartZ=0 EndX=5 EndY=-110 EndZ=0
    g11: LineSegment StartX=5 StartY=-110 StartZ=0 EndX=5 EndY=-5 EndZ=0
  constraints (25):
    c: Coincident(g0,g1)
    c: Coincident(g1,g2)
    c: Coincident(g2,g3)
    c: Coincident(g3,g0)
    c: Horizontal(g0)
    c: Horizontal(g2)
    c: Vertical(g1)
    c: Vertical(g3)
    c: Coincident(g0,g-1)
    c: Horizontal(g4)
    c: Coincident(g5,g4)
    c: Vertical(g5)
    c: Coincident(g6,g5)
    c: Horizontal(g6)
    c: Coincident(g7,g6)
    c: Vertical(g7)
    c: Coincident(g8,g7)
    c: Horizontal(g8)
    c: Coincident(g9,g8)
    c: Vertical(g9)
    c: Coincident(g10,g9)
    c: Horizontal(g10)
    c: Coincident(g11,g10)
    c: Coincident(g11,g4)
    c: Vertical(g11)
FEATURE [PartDesign::Pad] Pad021
  BaseFeature = -> Pad010
  Length = 5.67
  Length2 = 100
  Profile = -> Sketch024
  Type = 0
FEATURE [Sketcher::SketchObject] Sketch025
  MapMode = 5
  Placement = pos=(0,0,16.67) rot=(0,0,1;0rad)
  Support = -> [Pad021]
  sketch-geometry (12):
    g0: LineSegment StartX=0 StartY=-120 StartZ=0 EndX=95 EndY=-120 EndZ=0
    g1: LineSegment StartX=95 StartY=-120 StartZ=0 EndX=95 EndY=-42.5 EndZ=0
    g2: LineSegment StartX=80 StartY=-42.5 StartZ=0 EndX=15 EndY=-42.5 EndZ=0
    g3: LineSegment StartX=0 StartY=-42.5 StartZ=0 EndX=0 EndY=-120 EndZ=0
    g4: LineSegment StartX=15 StartY=-42.5 StartZ=0 EndX=15 EndY=-10 EndZ=0
    g5: LineSegment StartX=15 StartY=0 StartZ=0 EndX=0 EndY=0 EndZ=0
    g6: LineSegment StartX=0 StartY=0 StartZ=0 EndX=0 EndY=-42.5 EndZ=0
    g7: LineSegment StartX=15 StartY=0 StartZ=0 EndX=95 EndY=0 EndZ=0
    g8: LineSegment StartX=95 StartY=0 StartZ=0 EndX=95 EndY=-10 EndZ=0
    g9: LineSegment StartX=80 StartY=-10 StartZ=0 EndX=15 EndY=-10 EndZ=0
    g10: LineSegment StartX=80 StartY=-10 StartZ=0 EndX=80 EndY=-42.5 EndZ=0
    g11: LineSegment StartX=95 StartY=-42.5 StartZ=0 EndX=95 EndY=-10 EndZ=0
  constraints (21):
    c: Coincident(g0,g1)
    c: Coincident(g3,g0)
    c: Horizontal(g0)
    c: Horizontal(g2)
    c: Vertical(g1)
    c: Vertical(g3)
    c: PointOnObject(g0,g-2)
    c: Coincident(g5,g6)
    c: Horizontal(g5)
    c: Vertical(g4)
    c: Vertical(g6)
    c: Coincident(g6,g3)
    c: Coincident(g7,g8)
    c: Horizontal(g7)
    c: Horizontal(g9)
    c: Vertical(g8)
    c: Coincident(g7,g5)
    c: Vertical(g10)
    c: Vertical(g11)
    c: PointOnObject(g4,g9)
    c: Coincident(g2,g10)
FEATURE [PartDesign::Pad] Pad022
  BaseFeature = -> Pad021
  Length = 2
  Length2 = 100
  Profile = -> Sketch025
  Type = 0
FEATURE [PartDesign::Fillet] Fillet004
  Base = -> Pad022 [Edge96,Edge123,Edge105,Edge124]
  BaseFeature = -> Pad022
  Radius = 3.5
FEATURE [App::DocumentObjectGroup] Group  label="Parts"
  Group = -> [Body003,Body002,_0x2_pin_header,RaspberryPiZeroW]
FEATURE [Sketcher::SketchObject] Sketch026
  MapMode = 5
  Support = -> [XY_Plane004]
  sketch-geometry (28):
    g0: LineSegment StartX=0.2 StartY=-0.2 StartZ=0 EndX=15 EndY=-0.2 EndZ=0
    g1: LineSegment StartX=15 StartY=-0.2 StartZ=0 EndX=15 EndY=-10 EndZ=0
    g2: LineSegment StartX=15 StartY=-10 StartZ=0 EndX=2.5 EndY=-10 EndZ=0
    g3: LineSegment StartX=0.2 StartY=-10 StartZ=0 EndX=0.2 EndY=-0.2 EndZ=0
    g4: LineSegment StartX=0.2 StartY=-32.3 StartZ=0 EndX=17.5 EndY=-32.3 EndZ=0
    g5: LineSegment StartX=17.5 StartY=-31.4128 StartZ=0 EndX=17.5 EndY=-22.5 EndZ=0
    g6: LineSegment StartX=17.5 StartY=-22.5 StartZ=0 EndX=2.5 EndY=-22.5 EndZ=0
    g7: LineSegment StartX=0.2 StartY=-22.5 StartZ=0 EndX=0.2 EndY=-32.3 EndZ=0
    g8: LineSegment StartX=57.5 StartY=-22.5 StartZ=0 EndX=64.8 EndY=-22.5 EndZ=0
    g9: LineSegment StartX=64.8 StartY=-22.5 StartZ=0 EndX=64.8 EndY=-32.3 EndZ=0
    g10: LineSegment StartX=64.8 StartY=-32.3 StartZ=0 EndX=60 EndY=-32.3 EndZ=0
    g11: LineSegment StartX=57.5 StartY=-31.4128 StartZ=0 EndX=57.5 EndY=-22.5 EndZ=0
    g12: LineSegment StartX=17.5 StartY=-32.3 StartZ=0 EndX=60 EndY=-32.3 EndZ=0
    g13: LineSegment StartX=57.5 StartY=-31.4128 StartZ=0 EndX=50 EndY=-31.4128 EndZ=0
    g14: LineSegment StartX=50 StartY=-31.4128 StartZ=0 EndX=50 EndY=-7.5 EndZ=0
    g15: LineSegment StartX=50 StartY=-2.5 StartZ=0 EndX=47.5 EndY=-2.5 EndZ=0
    g16: LineSegment StartX=47.5 StartY=-2.5 StartZ=0 EndX=47.5 EndY=-31.4128 EndZ=0
    g17: LineSegment StartX=64.8 StartY=-0.2 StartZ=0 EndX=50 EndY=-0.2 EndZ=0
    g18: LineSegment StartX=50 StartY=-0.2 StartZ=0 EndX=50 EndY=-2.5 EndZ=0
    g19: LineSegment StartX=50 StartY=-7.5 StartZ=0 EndX=64.8 EndY=-7.5 EndZ=0
    g20: LineSegment StartX=64.8 StartY=-7.5 StartZ=0 EndX=64.8 EndY=-0.2 EndZ=0
    g21: LineSegment StartX=0.2 StartY=-10 StartZ=0 EndX=0.2 EndY=-22.5 EndZ=0
    g22: LineSegment StartX=2.5 StartY=-22.5 StartZ=0 EndX=2.5 EndY=-10 EndZ=0
    g23: LineSegment StartX=47.5 StartY=-31.4128 StartZ=0 EndX=17.5 EndY=-31.4128 EndZ=0
    g24: Circle CenterX=3.49637 CenterY=-26.5008 CenterZ=0 NormalX=0 NormalY=0 NormalZ=1 AngleXU=0 Radius=1.2
    g25: Circle CenterX=3.48617 CenterY=-3.49274 CenterZ=0 NormalX=0 NormalY=0 NormalZ=1 AngleXU=0 Radius=1.2
    g26: Circle CenterX=61.5025 CenterY=-3.49308 CenterZ=0 NormalX=0 NormalY=0 NormalZ=1 AngleXU=0 Radius=1.2
    g27: Circle CenterX=61.5 CenterY=-26.5 CenterZ=0 NormalX=0 NormalY=0 NormalZ=1 AngleXU=0 Radius=1.2
  constraints (42):
    c: Coincident(g0,g1)
    c: Coincident(g1,g2)
    c: Horizontal(g0)
    c: Horizontal(g2)
    c: Vertical(g1)
    c: Vertical(g3)
    c: Coincident(g5,g6)
    c: Coincident(g7,g4)
    c: Horizontal(g4)
    c: Horizontal(g6)
    c: Vertical(g5)
    c: Vertical(g7)
    c: Coincident(g8,g9)
    c: Coincident(g9,g10)
    c: Coincident(g11,g8)
    c: Horizontal(g8)
    c: Horizontal(g10)
    c: Vertical(g9)
    c: Vertical(g11)
    c: Horizontal(g12)
    c: Horizontal(g13)
    c: Coincident(g12,g4)
    c: PointOnObject(g13,g11)
    c: Coincident(g15,g16)
    c: Horizontal(g15)
    c: Vertical(g14)
    c: Vertical(g16)
    c: PointOnObject(g16,g13)
    c: Coincident(g19,g20)
    c: Horizontal(g19)
    c: Vertical(g18)
    c: Vertical(g20)
    c: Vertical(g21)
    c: Vertical(g22)
    c: Tangent(g13,g23)
    c: PointOnObject(g14,g18)
    c: PointOnObject(g18,g15)
    c: Coincident(g2,g22)
    c: Radius(g27) = 1.2
    c: Radius(g26) = 1.2
    c: Radius(g25) = 1.2
    c: Radius(g24) = 1.2
FEATURE [PartDesign::Pad] Pad023
  Length = 1.67
  Length2 = 100
  Profile = -> Sketch026
  Type = 0
FEATURE [Sketcher::SketchObject] Sketch027
  MapMode = 5
  Placement = pos=(0,0,1.67) rot=(0,0,1;0rad)
  Support = -> [Pad023]
  sketch-geometry (24):
    g0: LineSegment StartX=-1.25 StartY=1.25 StartZ=0 EndX=18.75 EndY=1.25 EndZ=0
    g1: LineSegment StartX=18.75 StartY=0 StartZ=0 EndX=18.75 EndY=-12.5 EndZ=0
    g2: LineSegment StartX=-1.25 StartY=-12.5 StartZ=0 EndX=-1.25 EndY=1.25 EndZ=0
    g3: LineSegment StartX=18.75 StartY=1.25 StartZ=0 EndX=46.25 EndY=1.25 EndZ=0
    g4: LineSegment StartX=46.25 StartY=0 StartZ=0 EndX=18.75 EndY=0 EndZ=0
    g5: LineSegment StartX=46.25 StartY=1.25 StartZ=0 EndX=66.25 EndY=1.25 EndZ=0
    g6: LineSegment StartX=66.25 StartY=1.25 StartZ=0 EndX=66.25 EndY=-11.25 EndZ=0
    g7: LineSegment StartX=46.25 StartY=-11.25 StartZ=0 EndX=46.25 EndY=0 EndZ=0
    g8: LineSegment StartX=46.25 StartY=-11.25 StartZ=0 EndX=46.25 EndY=-17.5 EndZ=0
    g9: LineSegment StartX=66.25 StartY=-18.75 StartZ=0 EndX=66.25 EndY=-33.75 EndZ=0
    g10: LineSegment StartX=66.25 StartY=-18.75 StartZ=0 EndX=66.25 EndY=-11.25 EndZ=0
    g11: Circle CenterX=61.25 CenterY=-15 CenterZ=0 NormalX=0 NormalY=0 NormalZ=1 AngleXU=0 Radius=2.5
    g12: Circle CenterX=53.75 CenterY=-21.25 CenterZ=0 NormalX=0 NormalY=0 NormalZ=1 AngleXU=0 Radius=2.5
    g13: LineSegment StartX=46.25 StartY=-17.5 StartZ=0 EndX=46.25 EndY=-33.75 EndZ=0
    g14: LineSegment StartX=-1.25 StartY=-12.5 StartZ=0 EndX=-1.25 EndY=-33.75 EndZ=0
    g15: LineSegment StartX=18.75 StartY=-33.75 StartZ=0 EndX=18.75 EndY=-12.5 EndZ=0
    g16: LineSegment StartX=18.75 StartY=-33.75 StartZ=0 EndX=46.25 EndY=-33.75 EndZ=0
    g17: LineSegment StartX=66.25 StartY=-33.75 StartZ=0 EndX=66.25 EndY=-38.75 EndZ=0
    g18: LineSegment StartX=66.25 StartY=-38.75 StartZ=0 EndX=-1.25 EndY=-38.75 EndZ=0
    g19: LineSegment StartX=-1.25 StartY=-38.75 StartZ=0 EndX=-1.25 EndY=-33.75 EndZ=0
    g20: LineSegment StartX=2.5 StartY=-11.25 StartZ=0 EndX=13.75 EndY=-11.25 EndZ=0
    g21: LineSegment StartX=13.75 StartY=-11.25 StartZ=0 EndX=13.75 EndY=-22.5 EndZ=0
    g22: LineSegment StartX=13.75 StartY=-22.5 StartZ=0 EndX=2.5 EndY=-22.5 EndZ=0
    g23: LineSegment StartX=2.5 StartY=-22.5 StartZ=0 EndX=2.5 EndY=-11.25 EndZ=0
  constraints (36):
    c: Coincident(g2,g0)
    c: Horizontal(g0)
    c: Vertical(g1)
    c: Vertical(g2)
    c: Horizontal(g3)
    c: Horizontal(g4)
    c: Coincident(g3,g0)
    c: Coincident(g5,g6)
    c: Horizontal(g5)
    c: Vertical(g6)
    c: Vertical(g7)
    c: Coincident(g5,g3)
    c: Vertical(g8)
    c: Vertical(g9)
    c: Vertical(g10)
    c: Vertical(g13)
    c: Vertical(g14)
    c: Vertical(g15)
    c: Coincident(g17,g18)
    c: Coincident(g18,g19)
    c: Horizontal(g16)
    c: Horizontal(g18)
    c: Vertical(g17)
    c: Vertical(g19)
    c: Coincident(g20,g21)
    c: Coincident(g21,g22)
    c: Coincident(g22,g23)
    c: Coincident(g23,g20)
    c: Horizontal(g20)
    c: Horizontal(g22)
    c: Vertical(g21)
    c: Vertical(g23)
    c: PointOnObject(g16,g15)
    c: PointOnObject(g16,g13)
    c: PointOnObject(g7,g4)
    c: PointOnObject(g1,g4)
FEATURE [PartDesign::Pad] Pad024
  BaseFeature = -> Pad023
  Length = 1
  Length2 = 100
  Profile = -> Sketch027
  Type = 0
FEATURE [PartDesign::Fillet] Fillet005
  Base = -> Pad024 [Face60]
  BaseFeature = -> Pad024
  Radius = 0.5
FEATURE [PartDesign::Body] Body004  label="FacePlate"
  Group = -> [Sketch026,Pad023,Sketch027,Pad024,Fillet005]
  Origin = -> Origin004
  Placement = pos=(0,0,14) rot=(0,0,1;0rad)
  Tip = -> Fillet005
FEATURE [Part::Part2DObjectPython] ShapeString  # Draft 2D object (typed FeaturePython)
  FontFile = <userpath>/Downloads/Open_Sans/OpenSans-SemiBold.ttf
  Placement = pos=(-40,40.03,-8) rot=(0,0,1;0rad)
  Size = 7
  String = CY PI
  Tracking = 0
FEATURE [Part::Extrusion] Extrude002
  Base = -> ShapeString
  Dir = (0,0,1)
  DirMode = 2
  FaceMakerClass = Part::FaceMakerBullseye
  LengthFwd = 0.5
  LengthRev = 0
  Placement = pos=(14.4118,-44.5,-17.1593) rot=(0,1,0;3.14159rad)
  Solid = false
  Symmetric = false
FEATURE [Part::Part2DObjectPython] ShapeString001  # Draft 2D object (typed FeaturePython)
  FontFile = <userpath>/Downloads/Open_Sans/OpenSans-Italic.ttf
  Placement = pos=(-30,30,-8) rot=(0,0,1;0rad)
  Size = 6
  String = > Zer0 Term
  Support = -> [Pocket004]
  Tracking = 0
FEATURE [Part::Extrusion] Extrude
  Base = -> ShapeString001
  Dir = (0,0,1)
  DirMode = 2
  FaceMakerClass = Part::FaceMakerBullseye
  LengthFwd = 0.5
  LengthRev = 0
  Placement = pos=(24,-43,-17) rot=(0,1,0;3.14159rad)
  Solid = false
  Symmetric = false
FEATURE [Sketcher::SketchObject] Sketch028
  MapMode = 5
  Placement = pos=(0,5,-1.33e-14) rot=(-1,0,0;1.5708rad)
  Support = -> [Pocket004]
  sketch-geometry (8):
    g0: LineSegment StartX=-8.75 StartY=5 StartZ=0 EndX=-10 EndY=5 EndZ=0
    g1: LineSegment StartX=-10 StartY=5 StartZ=0 EndX=-10 EndY=-100 EndZ=0
    g2: LineSegment StartX=-10 StartY=-100 StartZ=0 EndX=-8.75 EndY=-100 EndZ=0
    g3: LineSegment StartX=-8.75 StartY=-100 StartZ=0 EndX=-8.75 EndY=5 EndZ=0
    g4: LineSegment StartX=73.75 StartY=5 StartZ=0 EndX=75 EndY=5 EndZ=0
    g5: LineSegment StartX=75 StartY=5 StartZ=0 EndX=75 EndY=-100 EndZ=0
    g6: LineSegment StartX=75 StartY=-100 StartZ=0 EndX=73.75 EndY=-100 EndZ=0
    g7: LineSegment StartX=73.75 StartY=-100 StartZ=0 EndX=73.75 EndY=5 EndZ=0
  constraints (16):
    c: Coincident(g0,g1)
    c: Coincident(g1,g2)
    c: Coincident(g2,g3)
    c: Coincident(g3,g0)
    c: Horizontal(g0)
    c: Horizontal(g2)
    c: Vertical(g1)
    c: Vertical(g3)
    c: Coincident(g4,g5)
    c: Coincident(g5,g6)
    c: Coincident(g6,g7)
    c: Coincident(g7,g4)
    c: Horizontal(g4)
    c: Horizontal(g6)
    c: Vertical(g5)
    c: Vertical(g7)
FEATURE [PartDesign::Pocket] Pocket005
  BaseFeature = -> Pocket004
  Length = 5
  Length2 = 100
  Placement = pos=(0,0,0) rot=(1,0,0;1.5708rad)
  Profile = -> Sketch028
  Type = 0
FEATURE [Sketcher::SketchObject] Sketch029
  MapMode = 5
  Placement = pos=(0,0,0) rot=(1,0,0;3.14159rad)
  Support = -> [Fillet004]
  sketch-geometry (8):
    g0: LineSegment StartX=8.75 StartY=5 StartZ=0 EndX=7.5 EndY=5 EndZ=0
    g1: LineSegment StartX=7.5 StartY=5 StartZ=0 EndX=7.5 EndY=110 EndZ=0
    g2: LineSegment StartX=7.5 StartY=110 StartZ=0 EndX=8.75 EndY=110 EndZ=0
    g3: LineSegment StartX=8.75 StartY=110 StartZ=0 EndX=8.75 EndY=5 EndZ=0
    g4: LineSegment StartX=86.25 StartY=110 StartZ=0 EndX=87.5 EndY=110 EndZ=0
    g5: LineSegment StartX=87.5 StartY=110 StartZ=0 EndX=87.5 EndY=5 EndZ=0
    g6: LineSegment StartX=87.5 StartY=5 StartZ=0 EndX=86.25 EndY=5 EndZ=0
    g7: LineSegment StartX=86.25 StartY=5 StartZ=0 EndX=86.25 EndY=110 EndZ=0
  constraints (16):
    c: Coincident(g0,g1)
    c: Coincident(g1,g2)
    c: Coincident(g2,g3)
    c: Coincident(g3,g0)
    c: Horizontal(g0)
    c: Horizontal(g2)
    c: Vertical(g1)
    c: Vertical(g3)
    c: Coincident(g4,g5)
    c: Coincident(g5,g6)
    c: Coincident(g6,g7)
    c: Coincident(g7,g4)
    c: Horizontal(g4)
    c: Horizontal(g6)
    c: Vertical(g5)
    c: Vertical(g7)
FEATURE [PartDesign::Pocket] Pocket006
  BaseFeature = -> Fillet004
  Length = 5
  Length2 = 100
  Profile = -> Sketch029
  Type = 0
FEATURE [Sketcher::SketchObject] Sketch030
  MapMode = 5
  Placement = pos=(0,0,0) rot=(1,0,0;3.14159rad)
  Support = -> [Pocket006]
  sketch-geometry (4):
    g0: LineSegment StartX=12.5 StartY=5 StartZ=0 EndX=82.5 EndY=5 EndZ=0
    g1: LineSegment StartX=82.5 StartY=5 StartZ=0 EndX=82.5 EndY=0 EndZ=0
    g2: LineSegment StartX=82.5 StartY=0 StartZ=0 EndX=12.5 EndY=0 EndZ=0
    g3: LineSegment StartX=12.5 StartY=0 StartZ=0 EndX=12.5 EndY=5 EndZ=0
  constraints (8):
    c: Coincident(g0,g1)
    c: Coincident(g1,g2)
    c: Coincident(g2,g3)
    c: Coincident(g3,g0)
    c: Horizontal(g0)
    c: Horizontal(g2)
    c: Vertical(g1)
    c: Vertical(g3)
FEATURE [PartDesign::Pocket] Pocket007
  BaseFeature = -> Pocket006
  Length = 15
  Length2 = 100
  Profile = -> Sketch030
  Type = 0
FEATURE [PartDesign::Fillet] Fillet006
  Base = -> Pocket007 [Edge70,Edge72]
  BaseFeature = -> Pocket007
  Radius = 4
FEATURE [Sketcher::SketchObject] Sketch031
  MapMode = 5
  Placement = pos=(0,-3,3e-15) rot=(-1,0,0;1.5708rad)
  Support = -> [Pocket005]
  sketch-geometry (4):
    g0: LineSegment StartX=-2.5 StartY=5 StartZ=0 EndX=67.5 EndY=5 EndZ=0
    g1: LineSegment StartX=67.5 StartY=5 StartZ=0 EndX=67.5 EndY=10 EndZ=0
    g2: LineSegment StartX=67.5 StartY=10 StartZ=0 EndX=-2.5 EndY=10 EndZ=0
    g3: LineSegment StartX=-2.5 StartY=10 StartZ=0 EndX=-2.5 EndY=5 EndZ=0
  constraints (8):
    c: Coincident(g0,g1)
    c: Coincident(g1,g2)
    c: Coincident(g2,g3)
    c: Coincident(g3,g0)
    c: Horizontal(g0)
    c: Horizontal(g2)
    c: Vertical(g1)
    c: Vertical(g3)
FEATURE [PartDesign::Pad] Pad025
  BaseFeature = -> Pocket005
  Length = 15
  Length2 = 100
  Placement = pos=(0,0,0) rot=(1,0,0;1.5708rad)
  Profile = -> Sketch031
  Type = 0
FEATURE [PartDesign::Fillet] Fillet007
  Base = -> Pad025 [Edge170,Edge132]
  BaseFeature = -> Pad025
  Placement = pos=(0,0,0) rot=(1,0,0;1.5708rad)
  Radius = 4.2
FEATURE [Sketcher::SketchObject] Sketch032
  MapMode = 5
  Placement = pos=(0,0,11) rot=(1,0,0;3.14159rad)
  Support = -> [Fillet006]
  sketch-geometry (4):
    g0: LineSegment StartX=12.5 StartY=112.5 StartZ=0 EndX=82.5 EndY=112.5 EndZ=0
    g1: LineSegment StartX=82.5 StartY=112.5 StartZ=0 EndX=82.5 EndY=120 EndZ=0
    g2: LineSegment StartX=82.5 StartY=120 StartZ=0 EndX=12.5 EndY=120 EndZ=0
    g3: LineSegment StartX=12.5 StartY=120 StartZ=0 EndX=12.5 EndY=112.5 EndZ=0
  constraints (8):
    c: Coincident(g0,g1)
    c: Coincident(g1,g2)
    c: Coincident(g2,g3)
    c: Coincident(g3,g0)
    c: Horizontal(g0)
    c: Horizontal(g2)
    c: Vertical(g1)
    c: Vertical(g3)
FEATURE [PartDesign::Pocket] Pocket008
  BaseFeature = -> Fillet006
  Length = 4
  Length2 = 100
  Profile = -> Sketch032
  Type = 0
FEATURE [PartDesign::Body] Body001  label="Lid"
  Group = -> [Sketch011,Pad008,Sketch012,Pad009,Pad010,Sketch024,Pad021,Sketch025,Pad022,Fillet004,Sketch029,Pocket006,Sketch030,Pocket007,Fillet006,Sketch032,Pocket008]
  Origin = -> Origin001
  Placement = pos=(-15,10,-3) rot=(0,0,1;0rad)
  Tip = -> Pocket008
FEATURE [Sketcher::SketchObject] Sketch033
  MapMode = 5
  Placement = pos=(0,8,-2.53e-14) rot=(-1,0,0;1.5708rad)
  Support = -> [Fillet007]
  sketch-geometry (4):
    g0: LineSegment StartX=-2.5 StartY=-102.5 StartZ=0 EndX=67.5 EndY=-102.5 EndZ=0
    g1: LineSegment StartX=67.5 StartY=-102.5 StartZ=0 EndX=67.5 EndY=-110 EndZ=0
    g2: LineSegment StartX=67.5 StartY=-110 StartZ=0 EndX=-2.5 EndY=-110 EndZ=0
    g3: LineSegment StartX=-2.5 StartY=-110 StartZ=0 EndX=-2.5 EndY=-102.5 EndZ=0
  constraints (8):
    c: Coincident(g0,g1)
    c: Coincident(g1,g2)
    c: Coincident(g2,g3)
    c: Coincident(g3,g0)
    c: Horizontal(g0)
    c: Horizontal(g2)
    c: Vertical(g1)
    c: Vertical(g3)
FEATURE [PartDesign::Pad] Pad026
  BaseFeature = -> Fillet007
  Length = 3.9
  Length2 = 100
  Placement = pos=(0,0,0) rot=(1,0,0;1.5708rad)
  Profile = -> Sketch033
  Type = 0
FEATURE [PartDesign::Body] Body  label="Base"
  Group = -> [Sketch,Pad,Fillet,Sketch001,Pad001,Sketch002,Pocket,Sketch003,Pocket001,Sketch004,Pad002,Sketch005,Pad003,Sketch006,Pocket002,Fillet001,Sketch007,Sketch008,Pad004,Pad005,Pad006,Sketch009,Pocket003,Fillet002,Sketch010,Pad007,Sketch015,Pocket004,Sketch028,Pocket005,Sketch031,Pad025,Fillet007,Sketch033,Pad026]
  Origin = -> Origin
  Placement = pos=(0,0,0) rot=(1,0,0;1.5708rad)
  Tip = -> Pad026
FEATURE [App::DocumentObjectGroup] Group002  label="Base001"
  Group = -> [Extrude002,Body,Extrude]
FEATURE [Sketcher::SketchObject] Sketch034
  MapMode = 5
  Support = -> [XY_Plane005]
  sketch-geometry (14):
    g0: LineSegment StartX=0 StartY=5 StartZ=0 EndX=12.5 EndY=5 EndZ=0
    g1: LineSegment StartX=12.5 StartY=2.5 StartZ=0 EndX=12.5 EndY=-35 EndZ=0
    g2: LineSegment StartX=12.5 StartY=-35 StartZ=0 EndX=0 EndY=-35 EndZ=0
    g3: LineSegment StartX=0 StartY=-35 StartZ=0 EndX=0 EndY=5 EndZ=0
    g4: LineSegment StartX=12.5 StartY=5 StartZ=0 EndX=57.5 EndY=5 EndZ=0
    g5: LineSegment StartX=57.5 StartY=2.5 StartZ=0 EndX=12.5 EndY=2.5 EndZ=0
    g6: LineSegment StartX=57.5 StartY=5 StartZ=0 EndX=70 EndY=5 EndZ=0
    g7: LineSegment StartX=70 StartY=5 StartZ=0 EndX=70 EndY=-35 EndZ=0
    g8: LineSegment StartX=70 StartY=-35 StartZ=0 EndX=57.5 EndY=-35 EndZ=0
    g9: LineSegment StartX=57.5 StartY=-35 StartZ=0 EndX=57.5 EndY=2.5 EndZ=0
    g10: Circle CenterX=5.9967 CenterY=-5.50666 CenterZ=0 NormalX=0 NormalY=0 NormalZ=1 AngleXU=0 Radius=1.25
    g11: Circle CenterX=6.01299 CenterY=-28.4977 CenterZ=0 NormalX=0 NormalY=0 NormalZ=1 AngleXU=0 Radius=1.25
    g12: Circle CenterX=64.0158 CenterY=-28.5063 CenterZ=0 NormalX=0 NormalY=0 NormalZ=1 AngleXU=0 Radius=1.25
    g13: Circle CenterX=64.0016 CenterY=-5.50983 CenterZ=0 NormalX=0 NormalY=0 NormalZ=1 AngleXU=0 Radius=1.25
  constraints (25):
    c: Coincident(g1,g2)
    c: Coincident(g2,g3)
    c: Coincident(g3,g0)
    c: Horizontal(g0)
    c: Horizontal(g2)
    c: Vertical(g1)
    c: Vertical(g3)
    c: PointOnObject(g0,g-2)
    c: Horizontal(g4)
    c: Horizontal(g5)
    c: Coincident(g4,g0)
    c: Coincident(g6,g7)
    c: Coincident(g7,g8)
    c: Coincident(g8,g9)
    c: Horizontal(g6)
    c: Horizontal(g8)
    c: Vertical(g7)
    c: Vertical(g9)
    c: Coincident(g6,g4)
    c: Radius(g10) = 1.25
    c: Radius(g11) = 1.25
    c: Radius(g12) = 1.25
    c: Radius(g13) = 1.25
    c: PointOnObject(g1,g5)
    c: PointOnObject(g9,g5)
FEATURE [PartDesign::Pad] Pad027
  Length = 4
  Length2 = 100
  Profile = -> Sketch034
  Type = 0
FEATURE [Sketcher::SketchObject] Sketch035
  ExternalGeometry = -> [Pad027]
  MapMode = 5
  Placement = pos=(70,0,0) rot=(0.57735,0.57735,0.57735;2.0944rad)
  Support = -> [Pad027]
  sketch-geometry (8):
    g0: LineSegment StartX=5 StartY=4 StartZ=0 EndX=2.5 EndY=4 EndZ=0
    g1: LineSegment StartX=2.5 StartY=4 StartZ=0 EndX=2.5 EndY=5 EndZ=0
    g2: LineSegment StartX=5 StartY=4 StartZ=0 EndX=5 EndY=10 EndZ=0
    g3: ArcOfCircle CenterX=2.5 CenterY=10 CenterZ=0 NormalX=0 NormalY=0 NormalZ=1 AngleXU=0 Radius=2.5 StartAngle=-8e-15 EndAngle=1.58582
    g4: LineSegment StartX=2.5 StartY=5 StartZ=0 EndX=2.5 EndY=10 EndZ=0
    g5: LineSegment StartX=2.5 StartY=10 StartZ=0 EndX=-77.4922 EndY=7.82485 EndZ=0
    g6: ArcOfCircle CenterX=-77.5 CenterY=10.349 CenterZ=0 NormalX=0 NormalY=0 NormalZ=1 AngleXU=0 Radius=2.5242 StartAngle=3.28032 EndAngle=4.71552
    g7: LineSegment StartX=-80 StartY=10 StartZ=0 EndX=2.46244 EndY=12.4997 EndZ=0
  constraints (10):
    c: Coincident(g1,g0)
    c: Coincident(g2,g0)
    c: Coincident(g4,g1)
    c: Coincident(g4,g3)
    c: Coincident(g5,g3)
    c: Coincident(g6,g5)
    c: Coincident(g7,g6)
    c: Coincident(g7,g3)
    c: DistanceY(g0,g0) = 0
    c: DistanceY(g-3,g0) = 0
FEATURE [PartDesign::Pad] Pad028
  BaseFeature = -> Pad027
  Length = 70
  Length2 = 100
  Profile = -> Sketch035
  Reversed = true
  Type = 0
FEATURE [Sketcher::SketchObject] Sketch036
  MapMode = 5
  Placement = pos=(0,0,4) rot=(0,0,1;0rad)
  Support = -> [Pad028]
  sketch-geometry (4):
    g0: LineSegment StartX=11.25 StartY=10 StartZ=0 EndX=58.75 EndY=10 EndZ=0
    g1: LineSegment StartX=58.75 StartY=10 StartZ=0 EndX=58.75 EndY=-70 EndZ=0
    g2: LineSegment StartX=58.75 StartY=-70 StartZ=0 EndX=11.25 EndY=-70 EndZ=0
    g3: LineSegment StartX=11.25 StartY=-70 StartZ=0 EndX=11.25 EndY=10 EndZ=0
  constraints (8):
    c: Coincident(g0,g1)
    c: Coincident(g1,g2)
    c: Coincident(g2,g3)
    c: Coincident(g3,g0)
    c: Horizontal(g0)
    c: Horizontal(g2)
    c: Vertical(g1)
    c: Vertical(g3)
FEATURE [PartDesign::Pocket] Pocket009
  BaseFeature = -> Pad028
  Length = 50
  Length2 = 100
  Profile = -> Sketch036
  Reversed = true
  Type = 4
FEATURE [PartDesign::Fillet] Fillet008
  Base = -> Pocket009 [Face16,Face17,Face3,Face15,Face19,Edge24,Edge72,Edge28,Edge26,Edge73,Edge74,Edge21,Edge67]
  BaseFeature = -> Pocket009
  Radius = 1
FEATURE [Sketcher::SketchObject] Sketch037
  MapMode = 5
  Placement = pos=(0,0,4) rot=(0,0,1;0rad)
  Support = -> [Fillet008]
FEATURE [PartDesign::Body] Body005  label="Clip"
  Group = -> [Sketch034,Pad027,Sketch035,Pad028,Sketch036,Pocket009,Fillet008,Sketch037]
  Origin = -> Origin005
  Placement = pos=(67.5,2,-10) rot=(0,1,0;3.14159rad)
  Tip = -> Fillet008
FEATURE [App::DocumentObjectGroup] Group001  label="Case"
  Group = -> [Body001,Body004,Group002,Body005]
FEATURE [App::MeasureDistance] Distance  label="Distance: 49.08 mm"
  Distance = 49.0763
  P1 = (6.4,-15.64,22.251)
  P2 = (7.72218,4.46244,-22.4997)
FEATURE [App::MeasureDistance] Distance001  label="Distance: 12.61 mm"
  Distance = 12.6083
  P1 = (-1.5,4.46244,-22.4997)
  P2 = (-2.5,5.83013,-10.0058)
